# Revit family: QF_Macom_BRASEIRO50S-PB
name_source: partatom
category: Equipamento especial
units: mm (PartAtom-declared; Revit-internal decimal feet)

## family parameters
Com base no plano de trabalho = Não
Compartilhado = Não
Corte com vazios quando carregada = Não
Cota do conector redondo = Utilizar diâmetro
Número OmniClass = 23.40.40.14.17.11
Ponto de cálculo do ambiente = Não
Sempre na vertical = Sim
Tipo de parte = Normal
Título OmniClass = Cookers, Ovens, Stoves

## types (1)
- BRASEIRO50S-PB
    Cooking Temperature = 250 ºC to 350 ºC
    Depth = 997,000 mm
    Descrição = FORNO A CARVAO BRASEIRO MACOM DE SOBREPOR C/SUPORTE P/BANDEJAS, 1 GRELHA, CHAMINE, CORTA-CHAMA, PINCA, PORTA PRETO BRILHANTE
    Elevação padrão = 0,000 mm
    Exhaust Flow = 3800 m³/h
    Fabricante = MACOM
    Food Production Kg/h = 90 Kg/h
    Fuel Consumption = 12 - 16 Kg/day
    Fuel Type = Coal
    Heigth = 1355,000 mm
    Modelo = BRASEIRO50S-PB
    Show Clearances = Sim
    Show Logo = Sim
    URL = https://www.acosmacom.com.br
    Volume = 1,22 m³
    Weight = 310,00 kg
    Width = 925,000 mm

## geometry (parser evidence)
native form markers: Sweep x16
no freeform markers — native parametric forms only
